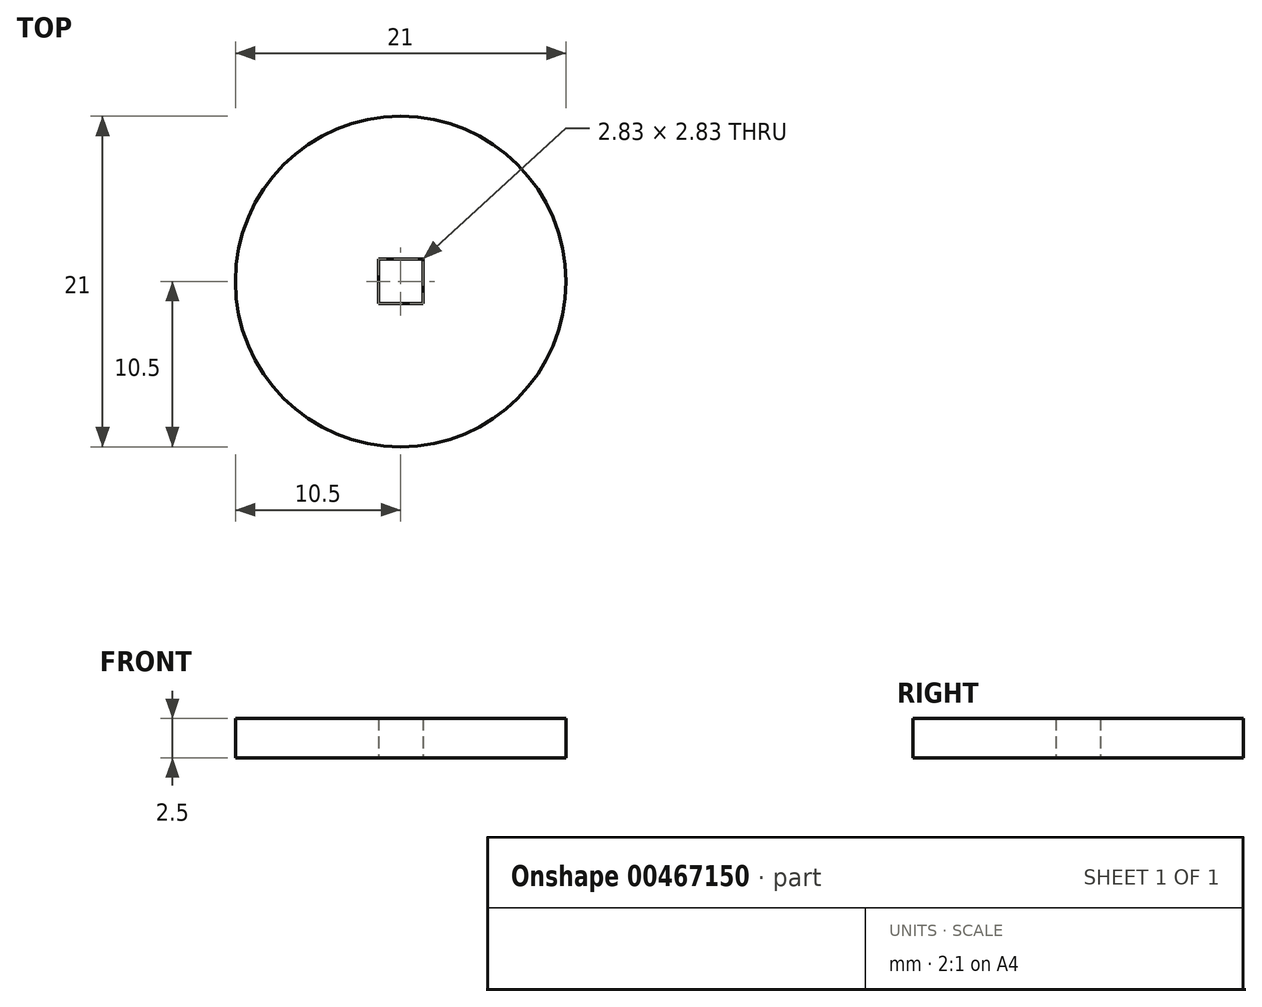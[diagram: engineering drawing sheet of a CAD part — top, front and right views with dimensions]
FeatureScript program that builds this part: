
annotation { "Feature Type Name" : "Feature", "Feature Type Description" : "" }
export const myFeature = defineFeature(function(context is Context, id is Id, definition is map)
    precondition{}
    {
        {
            var Q0;
            Q0=qCreatedBy(makeId("Top.planeOp"),FACE);
            var sketch = newSketch(context, id + "F0", { "sketchPlane" : qUnion([Q0])});
            skCircle(sketch, "E0", {"center": v(0, 0) * mm, "radius": 10.5 * mm});
            skCircle(sketch, "E1", {"center": v(0, 0) * mm, "radius": 2 * mm, "construction": true});
            skLineSegment(sketch, "E2.bottom", {"start": v(-1.41, 1.41) * mm, "end": v(1.41, 1.41) * mm});
            skLineSegment(sketch, "E2.top", {"start": v(-1.41, -1.41) * mm, "end": v(1.41, -1.41) * mm});
            skLineSegment(sketch, "E2.left", {"start": v(-1.41, 1.41) * mm, "end": v(-1.41, -1.41) * mm});
            skLineSegment(sketch, "E2.right", {"start": v(1.41, 1.41) * mm, "end": v(1.41, -1.41) * mm});
            skSolve(sketch);
        }
        {
            var Q0;
            Q0=makeQuery(id+"F0.imprint","IMPRINT",FACE,{"disambiguationData":[TD([[makeQuery(id+"F0.imprint","IMPRINT",EDGE,{"derivedFrom":sQuery(id+"F0.wireOp",EDGE,"E0")}),1.0]])]});
            extrude(context, id + "F1", {"entities" : qUnion([Q0]), "depth" : 2.5 * mm, "offsetDistance" : 25 * mm});
        }
    });
